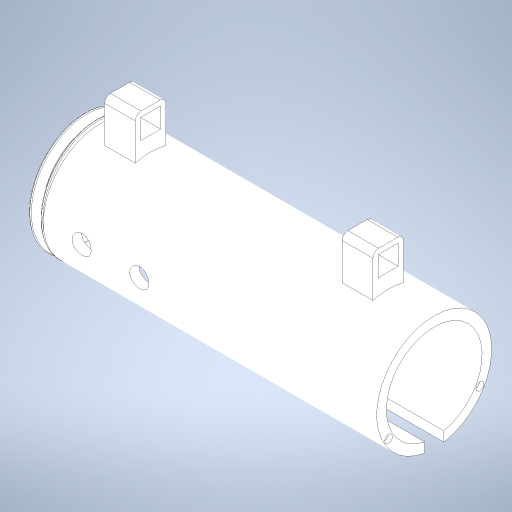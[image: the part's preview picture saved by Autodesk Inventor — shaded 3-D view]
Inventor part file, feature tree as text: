
AUTODESK INVENTOR PART (.ipt)
format: ipt  version: 2023 (Build 270158000, 158)  size: 495,104 bytes
history: native  units: in
note: dims shown in document units (in); Inventor stores cm internally (conversion verified against a paired STEP export)
features: sketch x7, extrude x6, pattern_linear x2, revolve x2, plane x1, fillet x1, mirror x1, thread x1, helix x1, projected_geometry x1
ambient origin geometry x8: Origin, YZ Plane, XZ Plane, XY Plane, X Axis, Y Axis, Z Axis, Center Point
bodies: Solid1 (feature_tree), Solid6 (feature_tree)
feature tree (23):
  sketch  "Sketch1"  dims[d0=1.1811in d1=0.9843in]
  extrude  "Extrusion1"  Depth=0.9843in
  extrude  "Extrusion2"  Depth=3.622in TaperAngle=0.0deg
  plane  "Work Plane1"
  extrude  "Extrusion4"  Depth=0.0984in
  extrude  "Extrusion5"  Depth=0.3937in
  pattern_linear  "Rectangular Pattern2"  Count1=11 Spacing1=0.0in
  fillet  "Fillet2"  Radius=0.315in
  extrude  "Extrusion6"  Depth=0.3937in
  pattern_linear  "Rectangular Pattern3"  Spacing1=0.1969in  [1 undecoded]
  extrude  "Extrusion7"  Depth=0.3937in TaperAngle=0.0deg
  mirror  "Mirror1"
  thread  "Thread7"  [1 undecoded]
  revolve  "Revolution9"  [1 undecoded]
  revolve  "Revolution10"  [1 undecoded]
  helix  "Coil5"  [1 undecoded]
  sketch  "Sketch6"  dims[d2=0.4921in d3=3.622in d4=0.0in]
  sketch  "Sketch7"  dims[d5=0.0984in d6=0.0in d19=0.0984in]
  sketch  "Sketch14"  dims[d20=0.0984in d21=0.3937in]
  projected_geometry  "Projected Loop1"
  sketch  "Sketch21"  dims[d22=1.1811in d23=0.9843in d24=0.4921in d25=0.0984in d26=0.0984in d27=4.3307in d28=0.0in]
  sketch  "Sketch22"  dims[d29=0.315in d30=0.315in d31=0.2067in d32=0.2067in d33=0.315in d34=0.0in]
  sketch  "Sketch23"  dims[d35=0.0591in d36=0.7874in d38=2.4409in d39=0.1969in d40=1.9685in d41=0.0in d42=0.5906in d43=0.7874in d45=0.5906in d59=0.3779in d81=0.3779in d94=120.0deg d95=0.0827in d96=0.0079in d97=0.0433in d98=0.0in d99=1.378in d109=0.3779in d130=0.3779in d142=0.1969in d143=0.0in d144=0.3779in d145=0.0189in d146=0.0189in d149=0.1181in d151=0.3779in d153=0.0in d154=0.0in d155=0.1182in d156=0.4331in d157=0.3937in d158=0.0in d159=0.0in d160=0.0in d161=0.0in d162=0.0in d100=0.0344in d101=0.0197in d102=0.0344in d103=0.0344in]
note: 5 required parameter values undecoded (feature->parameter linkage not recoverable at this tier; creation-order binding heuristic only, values carry confidence <= 0.55)